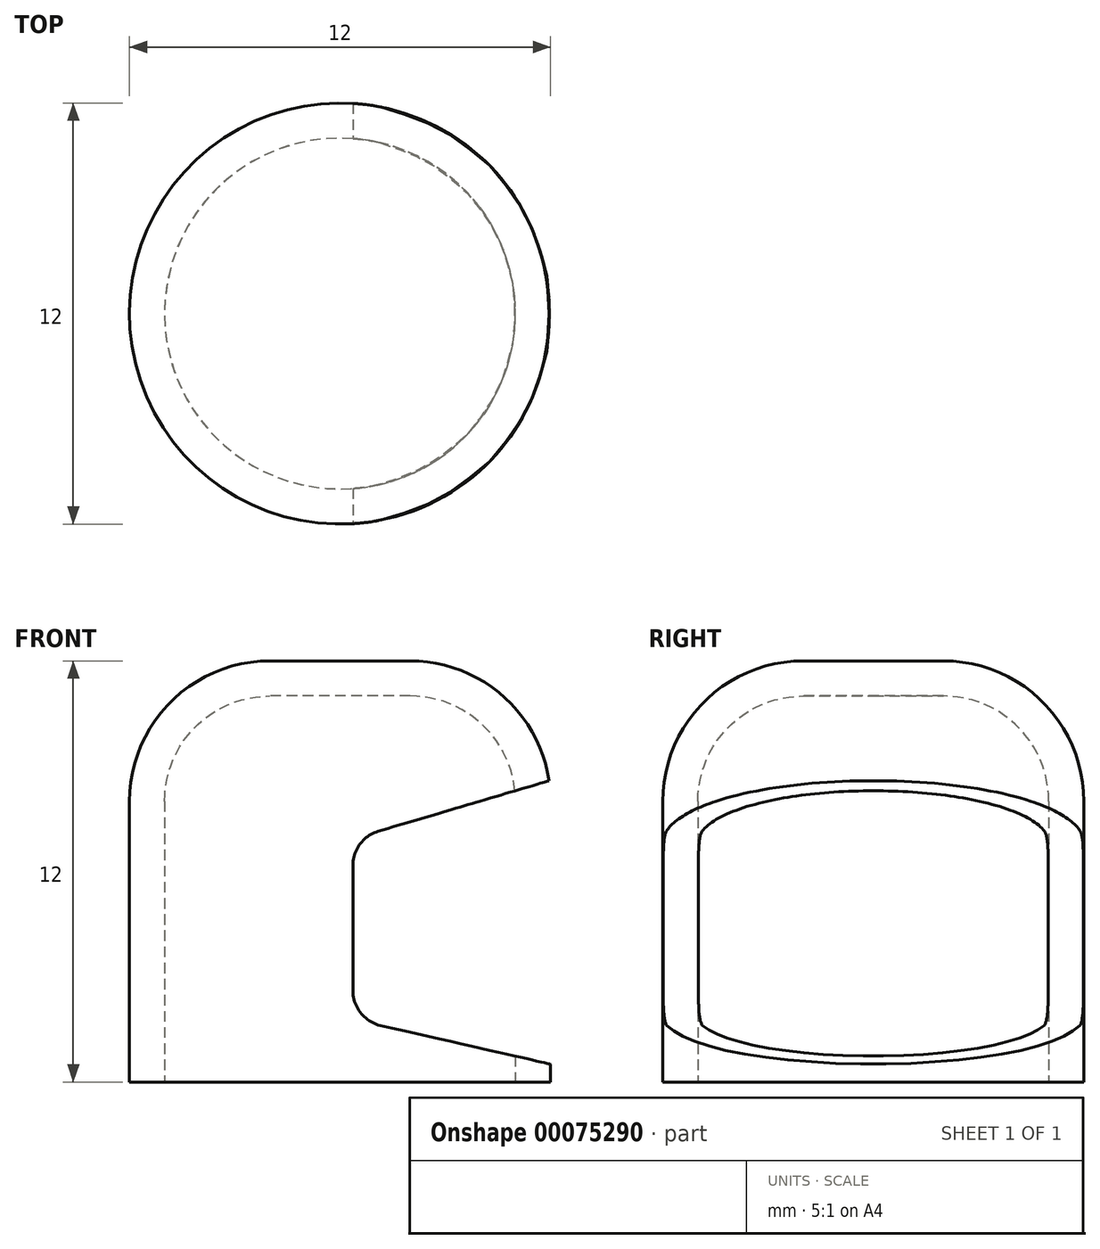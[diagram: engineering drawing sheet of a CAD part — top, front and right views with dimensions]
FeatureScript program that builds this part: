
annotation { "Feature Type Name" : "Feature", "Feature Type Description" : "" }
export const myFeature = defineFeature(function(context is Context, id is Id, definition is map)
    precondition{}
    {
        {
            var Q0;
            Q0=qCreatedBy(makeId("Top.planeOp"),FACE);
            var sketch = newSketch(context, id + "F0", { "sketchPlane" : qUnion([Q0])});
            skCircle(sketch, "E0", {"center": v(0, 0) * mm, "radius": 6 * mm});
            skSolve(sketch);
        }
        {
            var Q0;
            Q0 = qSketchRegion(id + "F0", true);
            extrude(context, id + "F1", {"entities" : qUnion([Q0]), "depth" : 12 * mm});
        }
        {
            var Q0;
            Q0=makeQuery(id+"F1.opExtrude","CAP_EDGE",EDGE,{"disambiguationData":[OSD([sQuery(id+"F0.wireOp",EDGE,"E0")])],"isStart":false});
            fillet(context, id + "F2", {"entities" : qUnion([Q0]), "radius" : 4 * mm, "tangentPropagation" : true, "allowEdgeOverflow" : false});
        }
        {
            var Q0;
            Q0=makeQuery(id+"F1.opExtrude","CAP_FACE",FACE,{"disambiguationData":[OSD([sQuery(id+"F0.wireOp",EDGE,"E0")])],"isStart":true});
            shell(context, id + "F3", {"entities" : qUnion([Q0]), "thickness" : 1 * mm});
        }
        {
            var Q0;
            Q0=qCreatedBy(makeId("Front.planeOp"),FACE);
            var sketch = newSketch(context, id + "F4", { "sketchPlane" : qUnion([Q0])});
            skLineSegment(sketch, "E1", {"start": v(6.24, 8.67) * mm, "end": v(1.08, 7.14) * mm});
            skLineSegment(sketch, "E2", {"start": v(0.37, 6.18) * mm, "end": v(0.37, 2.59) * mm});
            skLineSegment(sketch, "E3", {"start": v(1.15, 1.61) * mm, "end": v(6.33, 0.43) * mm});
            skLineSegment(sketch, "E4", {"start": v(6.33, 0.43) * mm, "end": v(6.24, 8.67) * mm});
            skPoint(sketch, "E5.visualSharp", {"position": v(0.37, 6.93) * mm});
            skArc(sketch, "E5.filletArc", {"start": v(1.08, 7.14) * mm, "mid": v(0.57, 6.78) * mm, "end": v(0.37, 6.18) * mm});
            skPoint(sketch, "E6.visualSharp", {"position": v(0.37, 1.79) * mm});
            skArc(sketch, "E6.filletArc", {"start": v(0.37, 2.59) * mm, "mid": v(0.59, 1.96) * mm, "end": v(1.15, 1.61) * mm});
            skSolve(sketch);
        }
        {
            var Q0;
            Q0=makeQuery(id+"F4.imprint","IMPRINT",FACE,{"disambiguationData":[TD([[makeQuery(id+"F4.imprint","IMPRINT",EDGE,{"derivedFrom":sQuery(id+"F4.wireOp",EDGE,"E1")}),1.0]])]});
            extrude(context, id + "F5", {"entities" : qUnion([Q0]), "operationType" : NewBodyOperationType.REMOVE, "endBound" : BoundingType.SYMMETRIC, "oppositeDirection" : true, "depth" : 25 * mm});
        }
    });
